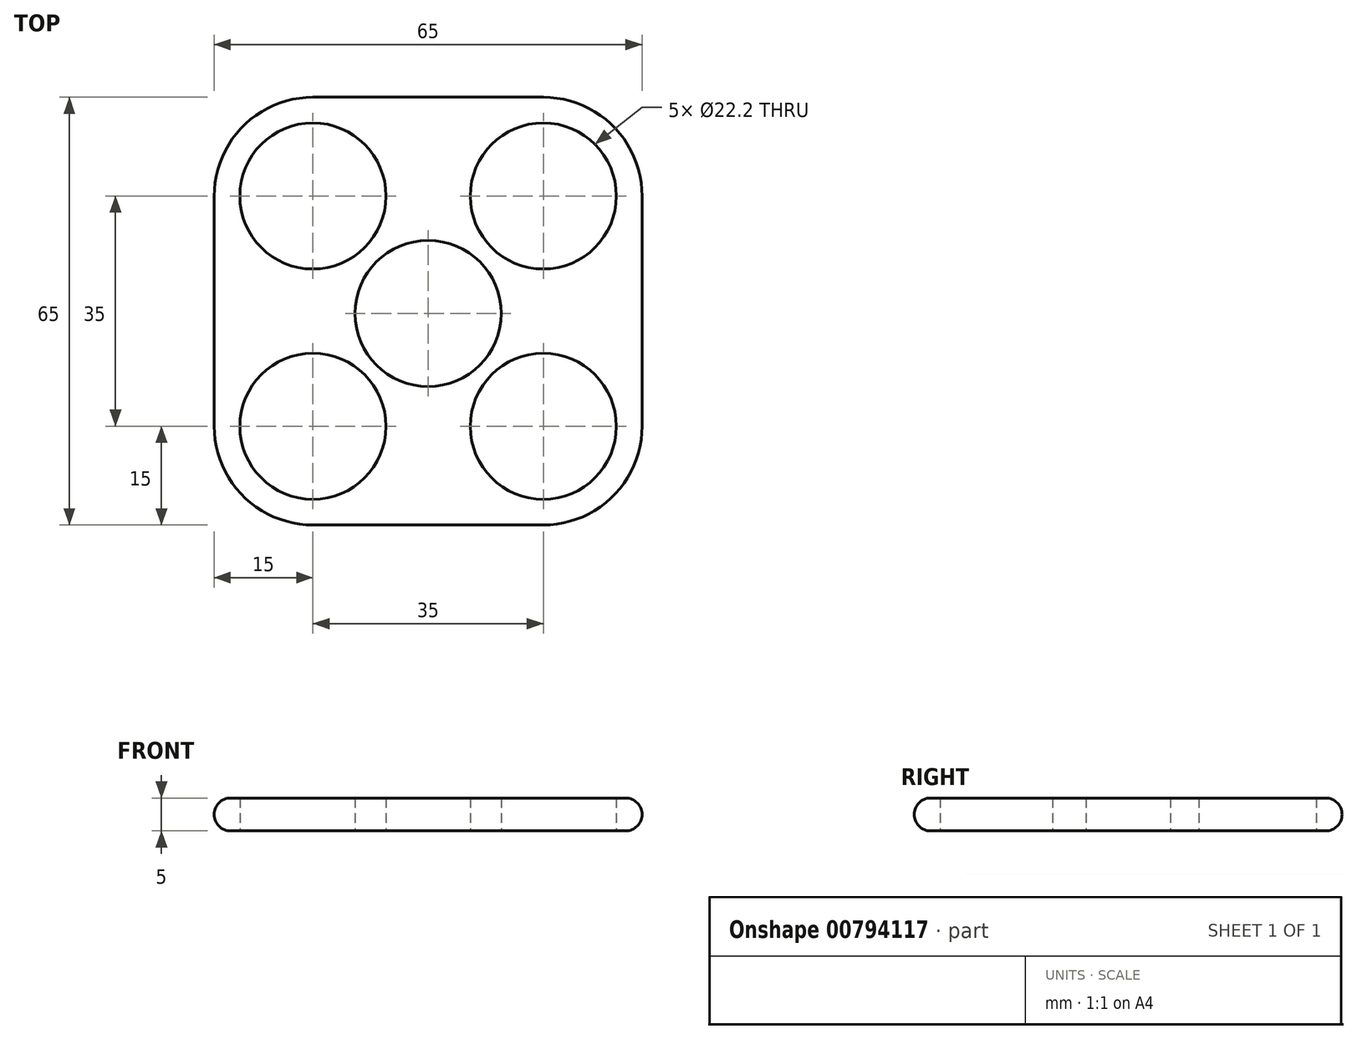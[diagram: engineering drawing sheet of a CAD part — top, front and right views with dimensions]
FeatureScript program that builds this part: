
annotation { "Feature Type Name" : "Feature", "Feature Type Description" : "" }
export const myFeature = defineFeature(function(context is Context, id is Id, definition is map)
    precondition{}
    {
        {
            var Q0;
            Q0=qCreatedBy(makeId("Top.planeOp"),FACE);
            var sketch = newSketch(context, id + "F0", { "sketchPlane" : qUnion([Q0])});
            skCircle(sketch, "E0", {"center": v(0, 0) * mm, "radius": 11.1 * mm});
            skCircle(sketch, "E1.0.1.0", {"center": v(0, 35) * mm, "radius": 11.1 * mm});
            skCircle(sketch, "E1.1.0.0", {"center": v(35, 0) * mm, "radius": 11.1 * mm});
            skCircle(sketch, "E1.1.1.0", {"center": v(35, 35) * mm, "radius": 11.1 * mm});
            skLineSegment(sketch, "E1.direction1", {"start": v(0, 0) * mm, "end": v(35, 0) * mm, "construction": true});
            skLineSegment(sketch, "E1.direction2", {"start": v(0, 0) * mm, "end": v(0, 35) * mm, "construction": true});
            skCircle(sketch, "E2", {"center": v(17.5, 17.15) * mm, "radius": 11.1 * mm});
            skLineSegment(sketch, "E3", {"start": v(35, 35) * mm, "end": v(35, 50) * mm});
            skLineSegment(sketch, "E4", {"start": v(35, 35) * mm, "end": v(50, 35) * mm});
            skArc(sketch, "E5", {"start": v(50, 35) * mm, "mid": v(45.6, 45.6) * mm, "end": v(35, 50) * mm});
            skPoint(sketch, "E6.orphan", {"position": v(50, 50) * mm});
            skLineSegment(sketch, "E7", {"start": v(0, 35) * mm, "end": v(0, 50) * mm});
            skLineSegment(sketch, "E8", {"start": v(0, 35) * mm, "end": v(-15, 35) * mm});
            skLineSegment(sketch, "E9", {"start": v(0, 0) * mm, "end": v(-15, 0) * mm});
            skLineSegment(sketch, "E10", {"start": v(0, 0) * mm, "end": v(0, -1.87) * mm});
            skLineSegment(sketch, "E11", {"start": v(35, 0) * mm, "end": v(35, -15) * mm});
            skLineSegment(sketch, "E12", {"start": v(35, 0) * mm, "end": v(50, 0) * mm});
            skLineSegment(sketch, "E13", {"start": v(0, 0) * mm, "end": v(0, -15) * mm});
            skArc(sketch, "E14", {"start": v(0, 50) * mm, "mid": v(-10.6, 45.6) * mm, "end": v(-15, 35) * mm});
            skArc(sketch, "E15", {"start": v(-15, 0) * mm, "mid": v(-10.6, -10.6) * mm, "end": v(0, -15) * mm});
            skArc(sketch, "E16", {"start": v(35, -15) * mm, "mid": v(45.6, -10.6) * mm, "end": v(50, 0) * mm});
            skLineSegment(sketch, "E17", {"start": v(-15, 35) * mm, "end": v(-15, 0) * mm});
            skLineSegment(sketch, "E18", {"start": v(50, 0) * mm, "end": v(50, 35) * mm});
            skLineSegment(sketch, "E19", {"start": v(35, 50) * mm, "end": v(0, 50) * mm});
            skLineSegment(sketch, "E20", {"start": v(0, -15) * mm, "end": v(35, -15) * mm});
            skSolve(sketch);
        }
        {
            var Q0;
            Q0=makeQuery(id+"F0.imprint","IMPRINT",FACE,{"disambiguationData":[TD([[makeQuery(id+"F0.imprint","IMPRINT",EDGE,{"derivedFrom":sQuery(id+"F0.wireOp",EDGE,"E2")}),-1.0]])]});
            var Q1;
            {var subQ5=sQuery(id+"F0.wireOp",EDGE,"E14");Q1=makeQuery(id+"F0.imprint","IMPRINT",FACE,{"disambiguationData":[TD([[makeQuery(id+"F0.imprint","IMPRINT",EDGE,{"derivedFrom":subQ5}),1.0]])]});}
            var Q2;
            {var subQ5=sQuery(id+"F0.wireOp",EDGE,"E15");Q2=makeQuery(id+"F0.imprint","IMPRINT",FACE,{"disambiguationData":[TD([[makeQuery(id+"F0.imprint","IMPRINT",EDGE,{"derivedFrom":subQ5}),1.0]])]});}
            var Q3;
            {var subQ5=sQuery(id+"F0.wireOp",EDGE,"E16");Q3=makeQuery(id+"F0.imprint","IMPRINT",FACE,{"disambiguationData":[TD([[makeQuery(id+"F0.imprint","IMPRINT",EDGE,{"derivedFrom":subQ5}),1.0]])]});}
            var Q4;
            {var subQ5=sQuery(id+"F0.wireOp",EDGE,"E5");Q4=makeQuery(id+"F0.imprint","IMPRINT",FACE,{"disambiguationData":[TD([[makeQuery(id+"F0.imprint","IMPRINT",EDGE,{"derivedFrom":subQ5}),1.0]])]});}
            extrude(context, id + "F1", {"entities" : qUnion([Q0, Q1, Q2, Q3, Q4]), "depth" : 5 * mm, "offsetDistance" : 25 * mm});
        }
        {
            var Q0;
            Q0=makeQuery(id+"F1.opExtrude","CAP_EDGE",EDGE,{"disambiguationData":[OSD([sQuery(id+"F0.wireOp",EDGE,"E17")])],"isStart":false});
            var Q1;
            Q1=makeQuery(id+"F1.opExtrude","CAP_EDGE",EDGE,{"disambiguationData":[OSD([sQuery(id+"F0.wireOp",EDGE,"E17")])],"isStart":true});
            fillet(context, id + "F2", {"entities" : qUnion([Q0, Q1]), "radius" : 2.5 * mm, "tangentPropagation" : true, "allowEdgeOverflow" : false});
        }
    });
